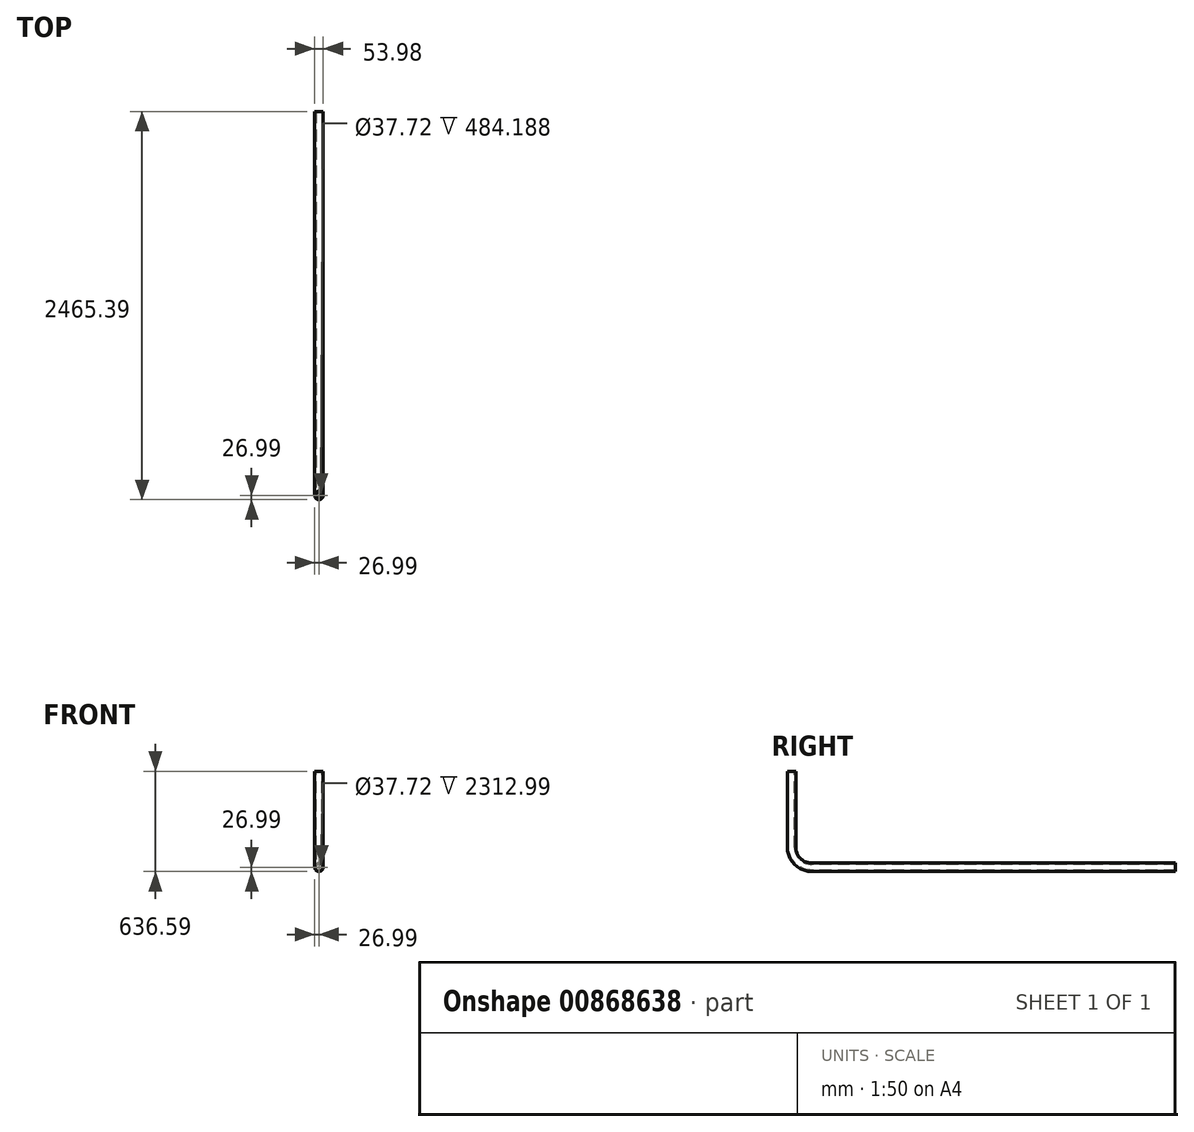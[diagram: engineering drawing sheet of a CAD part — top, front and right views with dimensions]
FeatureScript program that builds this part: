
annotation { "Feature Type Name" : "Feature", "Feature Type Description" : "" }
export const myFeature = defineFeature(function(context is Context, id is Id, definition is map)
    precondition{}
    {
        {
            var Q0;
            Q0=qCreatedBy(makeId("Right.planeOp"),FACE);
            var sketch = newSketch(context, id + "F0", { "sketchPlane" : qUnion([Q0])});
            skLineSegment(sketch, "E0", {"start": v(0, 125.41) * mm, "end": v(0, 609.6) * mm});
            skLineSegment(sketch, "E1", {"start": v(125.41, 0) * mm, "end": v(2438.4, 0) * mm});
            skPoint(sketch, "E2.visualSharp", {"position": v(0, 0) * mm});
            skArc(sketch, "E2.filletArc", {"start": v(0, 125.41) * mm, "mid": v(36.73, 36.73) * mm, "end": v(125.41, 0) * mm});
            skSolve(sketch);
        }
        {
            var Q0;
            Q0=sQuery(id+"F0.wireOp",VERTEX,"E1.end");
            var Q1;
            Q1=qCreatedBy(makeId("Front.planeOp"),FACE);
            cPlane(context, id + "F1", {"entities" : qUnion([Q0, Q1]), "cplaneType" : CPlaneType.PLANE_POINT, "offset" : 25.4 * mm, "width" : 152.4 * mm, "height" : 152.4 * mm});
        }
        {
            var Q0;
            Q0=qCreatedBy(id+"F1.planeOp",FACE);
            var sketch = newSketch(context, id + "F2", { "sketchPlane" : qUnion([Q0])});
            skCircle(sketch, "E3", {"center": v(0, 0) * mm, "radius": 18.86 * mm});
            skCircle(sketch, "E4", {"center": v(0, 0) * mm, "radius": 26.99 * mm});
            skSolve(sketch);
        }
        {
            var Q0;
            Q0=makeQuery(id+"F2.imprint","IMPRINT",FACE,{"disambiguationData":[TD([[makeQuery(id+"F2.imprint","IMPRINT",EDGE,{"derivedFrom":sQuery(id+"F2.wireOp",EDGE,"E3")}),-1.0]])]});
            var Q1;
            Q1=sQuery(id+"F0.wireOp",EDGE,"E1");
            var Q2;
            Q2=sQuery(id+"F0.wireOp",EDGE,"E2.filletArc");
            var Q3;
            Q3=sQuery(id+"F0.wireOp",EDGE,"E0");
            sweep(context, id + "F3", {"profiles" : qUnion([Q0]), "path" : qUnion([Q1, Q2, Q3])});
        }
    });
